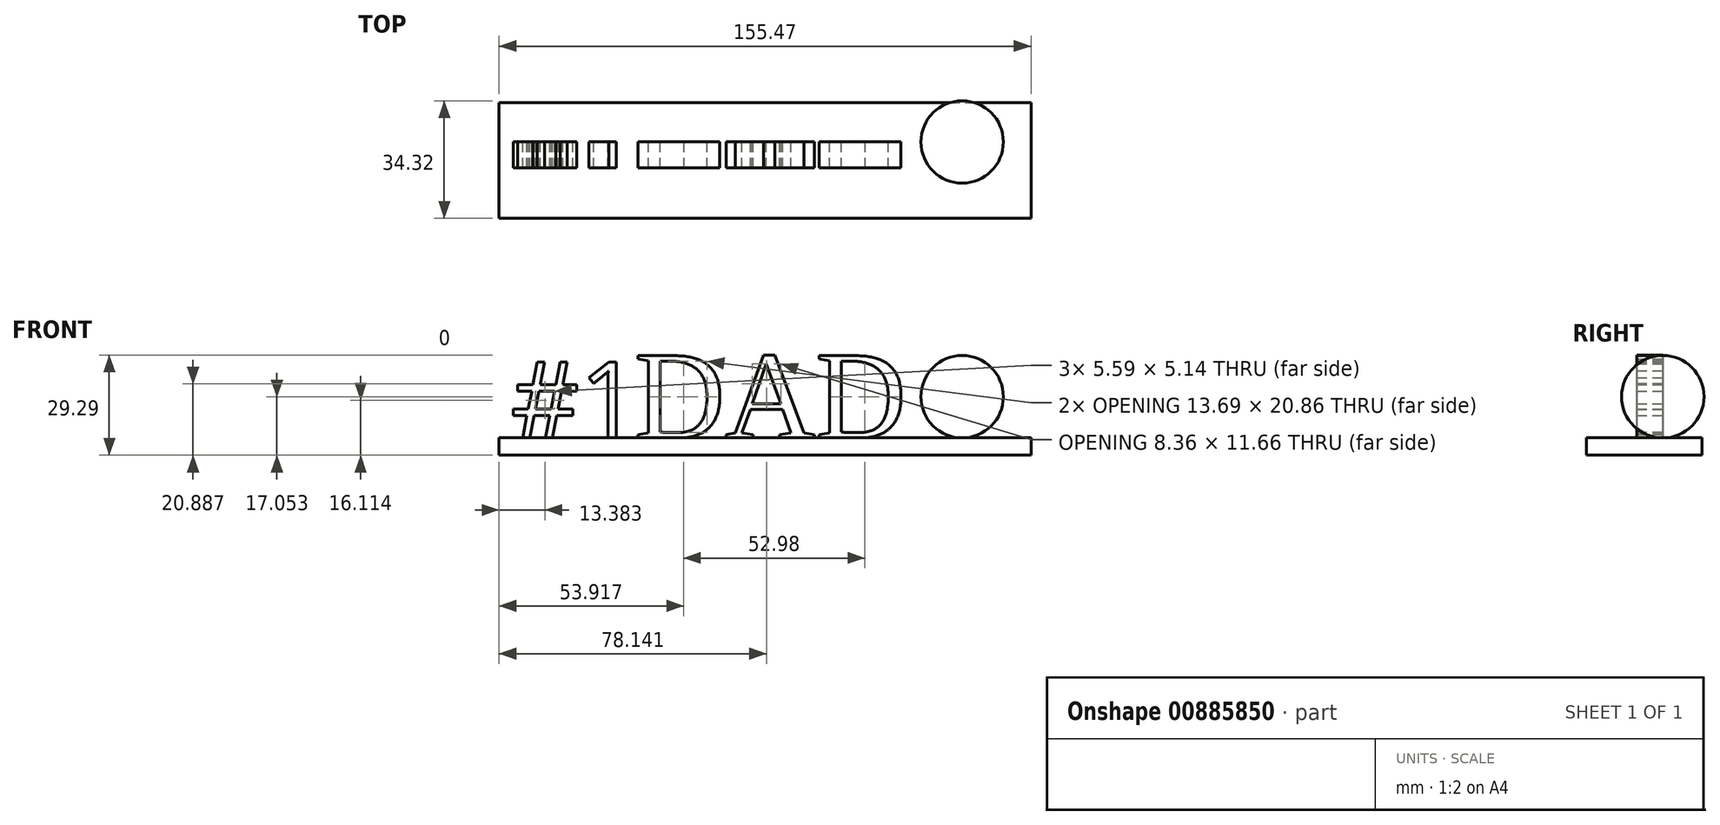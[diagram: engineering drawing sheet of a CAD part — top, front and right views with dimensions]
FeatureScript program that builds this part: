
annotation { "Feature Type Name" : "Feature", "Feature Type Description" : "" }
export const myFeature = defineFeature(function(context is Context, id is Id, definition is map)
    precondition{}
    {
        {
            var Q0;
            Q0=qCreatedBy(makeId("Top.planeOp"),FACE);
            var sketch = newSketch(context, id + "F0", { "sketchPlane" : qUnion([Q0])});
            skLineSegment(sketch, "E0.bottom", {"start": v(-65.32, 11.47) * mm, "end": v(90.15, 11.47) * mm});
            skLineSegment(sketch, "E0.top", {"start": v(-65.32, -22.28) * mm, "end": v(90.15, -22.28) * mm});
            skLineSegment(sketch, "E0.left", {"start": v(-65.32, 11.47) * mm, "end": v(-65.32, -22.28) * mm});
            skLineSegment(sketch, "E0.right", {"start": v(90.15, 11.47) * mm, "end": v(90.15, -22.28) * mm});
            skSolve(sketch);
        }
        {
            var Q0;
            Q0=makeQuery(id+"F0.imprint","IMPRINT",FACE,{"disambiguationData":[TD([[makeQuery(id+"F0.imprint","IMPRINT",EDGE,{"derivedFrom":sQuery(id+"F0.wireOp",EDGE,"E0.bottom")}),-1.0]])]});
            extrude(context, id + "F1", {"entities" : qUnion([Q0]), "depth" : 5.08 * mm, "offsetDistance" : 25.4 * mm});
        }
        {
            var Q0;
            Q0=qCreatedBy(makeId("Front.planeOp"),FACE);
            var sketch = newSketch(context, id + "F2", { "sketchPlane" : qUnion([Q0])});
            skText(sketch, "E1", { "text": "DAD", "fontName": "Tinos-Regular.ttf"});
            const initialGuessF2  = {"E1": [-0.02584, 0.00508, 1, 0, 0.02641]};
            skSetInitialGuess(sketch, initialGuessF2);
            skSolve(sketch);
        }
        {
            var Q0;
            Q0 = qSketchRegion(id + "F2", true);
            extrude(context, id + "F3", {"entities" : qUnion([Q0]), "operationType" : NewBodyOperationType.ADD, "depth" : 7.62 * mm, "offsetDistance" : 25.4 * mm});
        }
        {
            var Q0;
            Q0=qCreatedBy(makeId("Front.planeOp"),FACE);
            var sketch = newSketch(context, id + "F4", { "sketchPlane" : qUnion([Q0])});
            skText(sketch, "E2", { "text": "#1", "fontName": "OpenSans-Regular.ttf"});
            const initialGuessF4  = {"E2": [-0.06192, 0.00508, 1, 0, 0.02232]};
            skSetInitialGuess(sketch, initialGuessF4);
            skSolve(sketch);
        }
        {
            var Q0;
            Q0 = qSketchRegion(id + "F4", true);
            extrude(context, id + "F5", {"entities" : qUnion([Q0]), "depth" : 7.62 * mm, "offsetDistance" : 25.4 * mm});
        }
        {
            var Q0;
            Q0=qCreatedBy(makeId("Front.planeOp"),FACE);
            var sketch = newSketch(context, id + "F6", { "sketchPlane" : qUnion([Q0])});
            skArc(sketch, "E3", {"start": v(70.03, 29.16) * mm, "mid": v(57.98, 17.12) * mm, "end": v(70.03, 5.08) * mm});
            skLineSegment(sketch, "E4", {"start": v(70.03, 17.12) * mm, "end": v(70.03, 29.16) * mm});
            skLineSegment(sketch, "E5", {"start": v(70.03, 29.16) * mm, "end": v(70.03, 5.08) * mm});
            skSolve(sketch);
        }
        {
            var Q0;
            {var subQ0=sQuery(id+"F6.wireOp",EDGE,"E3");Q0=makeQuery(id+"F6.imprint","IMPRINT",FACE,{"disambiguationData":[TD([[makeQuery(id+"F6.imprint","IMPRINT",EDGE,{"derivedFrom":subQ0}),1.0]])]});}
            var Q1;
            Q1=sQuery(id+"F6.wireOp",EDGE,"E5");
            revolve(context, id + "F7", {"surfaceOperationType" : NewSurfaceOperationType.NEW, "entities" : qUnion([Q0]), "axis" : qUnion([Q1]), "revolveType" : RevolveType.FULL});
        }
    });
